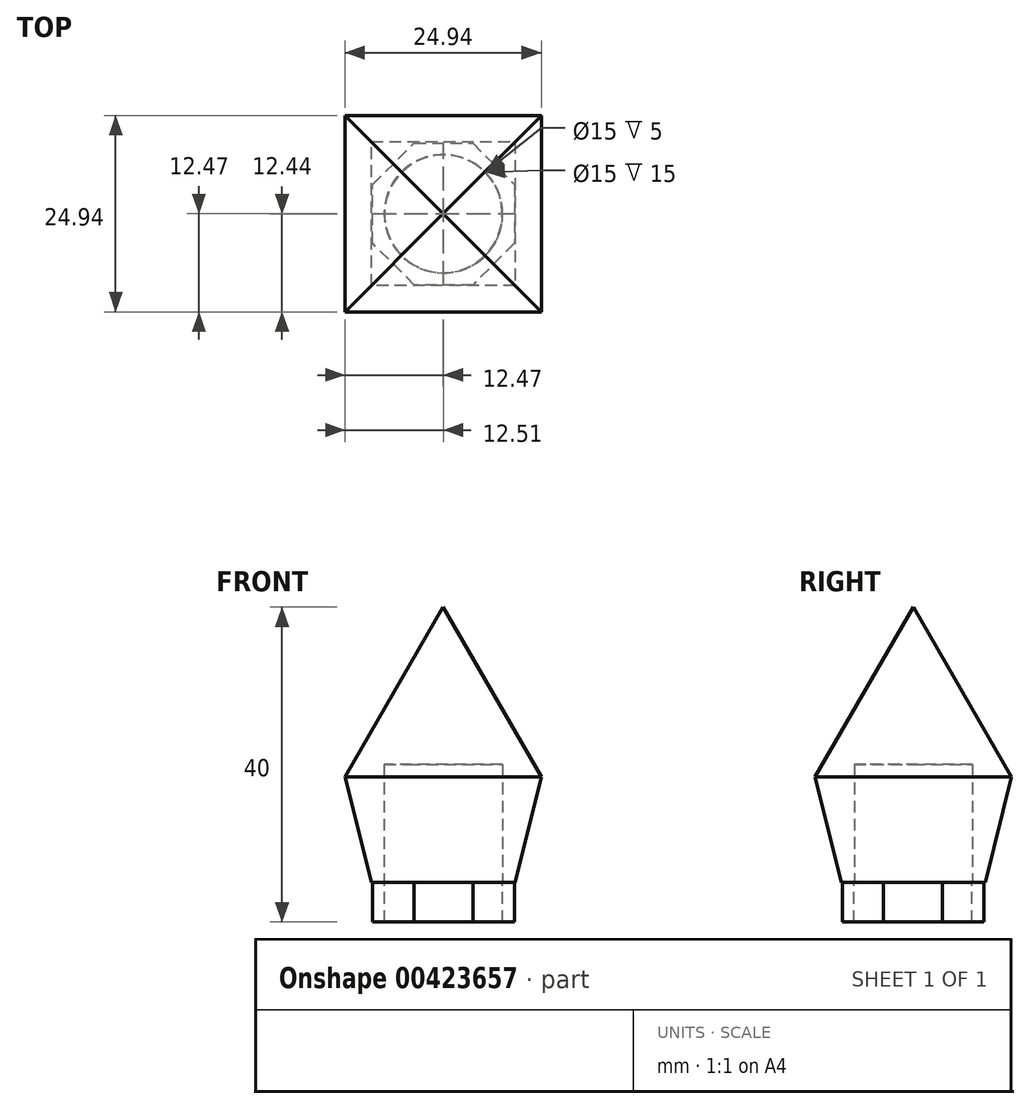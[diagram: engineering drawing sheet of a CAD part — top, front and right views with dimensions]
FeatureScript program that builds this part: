
annotation { "Feature Type Name" : "Feature", "Feature Type Description" : "" }
export const myFeature = defineFeature(function(context is Context, id is Id, definition is map)
    precondition{}
    {
        {
            var Q0;
            Q0=qCreatedBy(makeId("Top.planeOp"),FACE);
            var sketch = newSketch(context, id + "F0", { "sketchPlane" : qUnion([Q0])});
            skLineSegment(sketch, "E0.bottom", {"start": v(0, 0) * mm, "end": v(-25, 0) * mm});
            skLineSegment(sketch, "E0.top", {"start": v(0, -25) * mm, "end": v(-25, -25) * mm});
            skLineSegment(sketch, "E0.left", {"start": v(0, 0) * mm, "end": v(0, -25) * mm});
            skLineSegment(sketch, "E0.right", {"start": v(-25, 0) * mm, "end": v(-25, -25) * mm});
            skCircle(sketch, "E1", {"center": v(-12.5, -12.5) * mm, "radius": 7.5 * mm});
            skPoint(sketch, "E1.centerSnap0", {"position": v(-12.5, 0) * mm});
            skPoint(sketch, "E1.centerSnap1", {"position": v(0, -12.5) * mm});
            skSolve(sketch);
        }
        {
            var Q0;
            Q0=makeQuery(id+"F0.imprint","IMPRINT",FACE,{"disambiguationData":[TD([[makeQuery(id+"F0.imprint","IMPRINT",EDGE,{"derivedFrom":sQuery(id+"F0.wireOp",EDGE,"E0.bottom")}),1.0]])]});
            var Q1;
            Q1=makeQuery(id+"F0.imprint","IMPRINT",FACE,{"disambiguationData":[TD([[makeQuery(id+"F0.imprint","IMPRINT",EDGE,{"derivedFrom":sQuery(id+"F0.wireOp",EDGE,"E1")}),1.0]])]});
            extrude(context, id + "F1", {"entities" : qUnion([Q0, Q1]), "depth" : 35 * mm});
        }
        {
            var Q0;
            Q0=makeQuery(id+"F0.imprint","IMPRINT",FACE,{"disambiguationData":[TD([[makeQuery(id+"F0.imprint","IMPRINT",EDGE,{"derivedFrom":sQuery(id+"F0.wireOp",EDGE,"E1")}),1.0]])]});
            var Q1;
            Q1=sQuery(id+"F0.wireOp",EDGE,"E1");
            extrude(context, id + "F2", {"entities" : qUnion([Q0]), "operationType" : NewBodyOperationType.REMOVE, "surfaceEntities" : qUnion([Q1]), "depth" : 15 * mm});
        }
        {
            var Q0;
            Q0=makeQuery(id+"F1.opExtrude","CAP_EDGE",EDGE,{"disambiguationData":[OSD([sQuery(id+"F0.wireOp",EDGE,"E0.right")])],"isStart":false});
            var Q1;
            Q1=makeQuery(id+"F1.opExtrude","CAP_EDGE",EDGE,{"disambiguationData":[OSD([sQuery(id+"F0.wireOp",EDGE,"E0.top")])],"isStart":false});
            var Q2;
            Q2=makeQuery(id+"F1.opExtrude","CAP_EDGE",EDGE,{"disambiguationData":[OSD([sQuery(id+"F0.wireOp",EDGE,"E0.left")])],"isStart":false});
            var Q3;
            Q3=makeQuery(id+"F1.opExtrude","CAP_EDGE",EDGE,{"disambiguationData":[OSD([sQuery(id+"F0.wireOp",EDGE,"E0.bottom")])],"isStart":false});
            chamfer(context, id + "F3", {"entities" : qUnion([Q0, Q1, Q2, Q3]), "chamferType" : ChamferType.OFFSET_ANGLE, "width" : 12.5 * mm, "oppositeDirection" : false, "angle" : 60 * degree, "tangentPropagation" : true});
        }
        {
            var Q0;
            Q0=qCreatedBy(makeId("Top.planeOp"),FACE);
            var sketch = newSketch(context, id + "F4", { "sketchPlane" : qUnion([Q0])});
            skCircle(sketch, "E2.cCircle", {"center": v(-12.46, -12.53) * mm, "radius": 9 * mm, "construction": true});
            skLineSegment(sketch, "E2.0", {"start": v(-3.46, -8.8) * mm, "end": v(-3.46, -16.26) * mm});
            skLineSegment(sketch, "E2.1", {"start": v(-3.46, -16.26) * mm, "end": v(-8.73, -21.53) * mm});
            skLineSegment(sketch, "E2.2", {"start": v(-8.73, -21.53) * mm, "end": v(-16.19, -21.53) * mm});
            skLineSegment(sketch, "E2.3", {"start": v(-16.19, -21.53) * mm, "end": v(-21.46, -16.26) * mm});
            skLineSegment(sketch, "E2.4", {"start": v(-21.46, -16.26) * mm, "end": v(-21.46, -8.8) * mm});
            skLineSegment(sketch, "E2.5", {"start": v(-21.46, -8.8) * mm, "end": v(-16.19, -3.53) * mm});
            skLineSegment(sketch, "E2.6", {"start": v(-16.19, -3.53) * mm, "end": v(-8.73, -3.53) * mm});
            skLineSegment(sketch, "E2.7", {"start": v(-8.73, -3.53) * mm, "end": v(-3.46, -8.8) * mm});
            skPoint(sketch, "E2.0.midPoint", {"position": v(-3.46, -12.53) * mm});
            skCircle(sketch, "E3", {"center": v(-12.46, -12.53) * mm, "radius": 7.5 * mm});
            skSolve(sketch);
        }
        {
            var Q0;
            Q0=qSketchRegion(id+"F4",true);
            extrude(context, id + "F5", {"entities" : qUnion([Q0]), "operationType" : NewBodyOperationType.ADD, "oppositeDirection" : true, "depth" : 5 * mm});
        }
        {
            var Q0;
            Q0=makeQuery(id+"F1.opExtrude","CAP_EDGE",EDGE,{"disambiguationData":[OSD([sQuery(id+"F0.wireOp",EDGE,"E0.top")])],"isStart":true});
            var Q1;
            Q1=makeQuery(id+"F1.opExtrude","CAP_EDGE",EDGE,{"disambiguationData":[OSD([sQuery(id+"F0.wireOp",EDGE,"E0.left")])],"isStart":true});
            var Q2;
            Q2=makeQuery(id+"F1.opExtrude","CAP_EDGE",EDGE,{"disambiguationData":[OSD([sQuery(id+"F0.wireOp",EDGE,"E0.bottom")])],"isStart":true});
            var Q3;
            Q3=makeQuery(id+"F1.opExtrude","CAP_EDGE",EDGE,{"disambiguationData":[OSD([sQuery(id+"F0.wireOp",EDGE,"E0.right")])],"isStart":true});
            chamfer(context, id + "F6", {"entities" : qUnion([Q0, Q1, Q2, Q3]), "chamferType" : ChamferType.OFFSET_ANGLE, "width" : 13.5 * mm, "oppositeDirection" : true, "angle" : 14 * degree, "tangentPropagation" : true});
        }
    });
